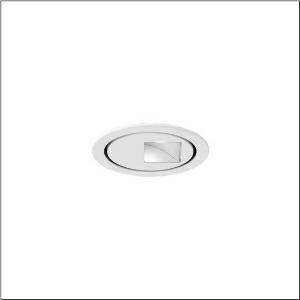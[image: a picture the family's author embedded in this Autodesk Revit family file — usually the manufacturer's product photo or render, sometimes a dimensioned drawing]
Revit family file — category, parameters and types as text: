
# Revit family: lunis_11_micro_round_51dj11b71wg21
name_source: partatom
category: Lighting Fixtures
units: mm (PartAtom-declared; Revit-internal decimal feet)

## family parameters
Cut with Voids When Loaded = No
Host = Face
Light Source = No
Part Type = Normal
Room Calculation Point = No
Round Connector Dimension = Use Diameter
Shared = No

## types (1)
- Lunis 11 micro round (1 x LED 4000K / CRI = 80 (unbekannt), 1400 lm, 4000K)
    Apparent Load = 20 VA
    CIE Flux Codes = 42 75 96 100 100
    Color Rendering = 80
    Color Temperature = 4000K
    Default Elevation = 1800 mm
    Description = Lunis 11 micro round, downlight, light control with wallwasher, of highly reflective aluminium, highly specular, light emission: direct distribution, LED rated luminous flux: 1.400lm, light colour: 840, with terminal, 3-pole, mains connection: 220..230V, AC, 50/60Hz, LED module, of aluminium, highly specular, white, diameter: 114mm, clamping range: 1..40mm, recessing ring, of plastic, traffic white (RAL 9016), protection rating (complete): IP20, insulation class (complete): insulation class II (safety insulation), certification: CE, permissible ambient temperature for indoor applications: 0..+35°C, packaging unit: 1 piece
    Height = 0 mm  [stored 0 ft]
    Lamp = 1 x LED 4000K / CRI >= 80 (unbekannt)
    Lamp Light Flux = 1400 lm
    Lamp count = 1
    Length = 114 mm
    Luminous efficacy = 71 lm/W
    Manufacturer = Siteco
    ModVariant = No
    Model = 51DJ11B71WG21
    Mounting Place = Ceiling
    Mounting Type = Recessed
    Number of Poles = 1
    OnlyDefault = Yes
    Power Factor = 1
    Product Name = Lunis 11 micro round
    Product group = downlight
    ProductGroupID = 401
    Protection Class = Protection class II
    Protection Degree = IP 20
    RLX_Detail_Level = 1
    RLX_Emergency_Light_Flux = 0 lm
    RLX_Emergency_Type = 0
    RLX_Emergency_Type_DB = No
    RlxData = <blob elided: 40501 chars, md5=597f2c68>
    Socket = socket
    Standby Power = 0 W
    System Light Flux = 1400 lm
    System Power = 20 W
    Type Comments = Product without accessories
    Type Image = l_1004773.jpg
    URL = http://relux.com
    VarID = ---
    Voltage = 0 V
    Weight = 0.00 kg
    Width = 114 mm

note: [stored X ft] marks values corroborated as IEEE doubles in the binary element streams (Revit-internal decimal feet)

## geometry (parser evidence)
native form markers: Blend x4, Sweep x10
no freeform markers — native parametric forms only
